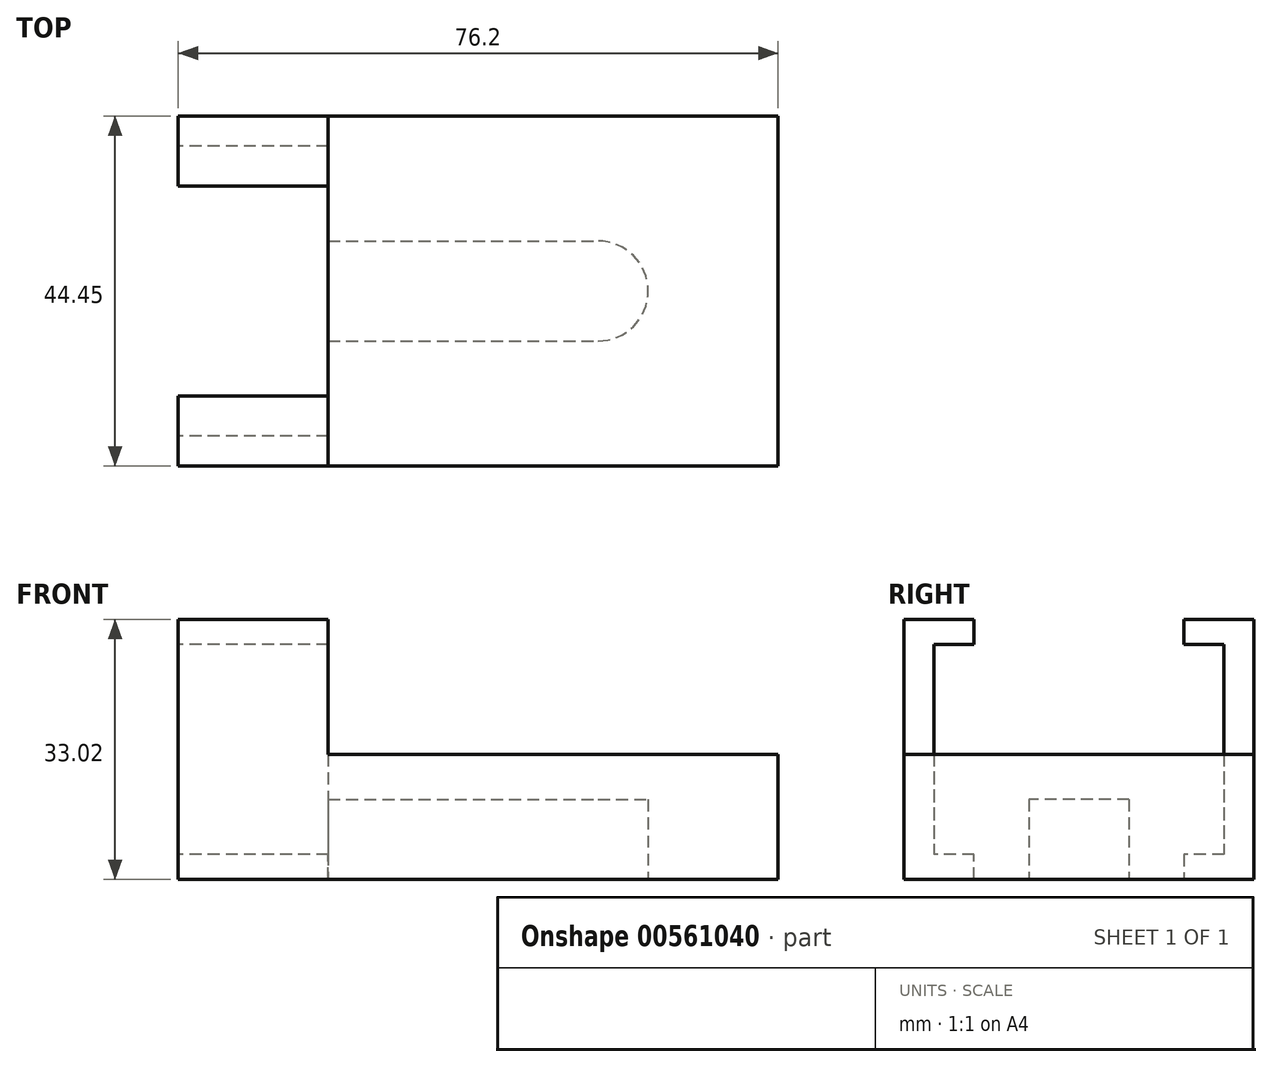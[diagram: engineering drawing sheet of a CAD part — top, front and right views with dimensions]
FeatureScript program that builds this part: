
annotation { "Feature Type Name" : "Feature", "Feature Type Description" : "" }
export const myFeature = defineFeature(function(context is Context, id is Id, definition is map)
    precondition{}
    {
        {
            var Q0;
            Q0=qCreatedBy(makeId("Top.planeOp"),FACE);
            var sketch = newSketch(context, id + "F0", { "sketchPlane" : qUnion([Q0])});
            skLineSegment(sketch, "E0", {"start": v(0, 0) * mm, "end": v(76.2, 0) * mm});
            skLineSegment(sketch, "E1", {"start": v(76.2, 0) * mm, "end": v(76.2, 44.45) * mm});
            skLineSegment(sketch, "E2", {"start": v(76.2, 44.45) * mm, "end": v(0, 44.45) * mm});
            skLineSegment(sketch, "E3", {"start": v(0, 44.45) * mm, "end": v(0, 0) * mm});
            skSolve(sketch);
        }
        {
            var Q0;
            Q0=makeQuery(id+"F0.imprint","IMPRINT",FACE,{"disambiguationData":[TD([[makeQuery(id+"F0.imprint","IMPRINT",EDGE,{"derivedFrom":sQuery(id+"F0.wireOp",EDGE,"E0")}),1.0]])]});
            extrude(context, id + "F1", {"entities" : qUnion([Q0]), "depth" : 33.02 * mm, "offsetDistance" : 25.4 * mm});
        }
        {
            var Q0;
            Q0=makeQuery(id+"F1.opExtrude","CAP_FACE",FACE,{"disambiguationData":[OSD([sQuery(id+"F0.wireOp",EDGE,"E0"),sQuery(id+"F0.wireOp",EDGE,"E1"),sQuery(id+"F0.wireOp",EDGE,"E2"),sQuery(id+"F0.wireOp",EDGE,"E3")])],"isStart":false});
            var sketch = newSketch(context, id + "F2", { "sketchPlane" : qUnion([Q0])});
            skLineSegment(sketch, "E4.bottom", {"start": v(76.2, 44.45) * mm, "end": v(19.05, 44.45) * mm});
            skLineSegment(sketch, "E4.top", {"start": v(76.2, 0) * mm, "end": v(19.05, 0) * mm});
            skLineSegment(sketch, "E4.left", {"start": v(76.2, 44.45) * mm, "end": v(76.2, 0) * mm});
            skLineSegment(sketch, "E4.right", {"start": v(19.05, 44.45) * mm, "end": v(19.05, 0) * mm});
            skSolve(sketch);
        }
        {
            var Q0;
            Q0=makeQuery(id+"F2.imprint","IMPRINT",FACE,{"disambiguationData":[TD([[makeQuery(id+"F2.imprint","IMPRINT",EDGE,{"derivedFrom":sQuery(id+"F2.wireOp",EDGE,"E4.bottom")}),1.0]])]});
            extrude(context, id + "F3", {"entities" : qUnion([Q0]), "operationType" : NewBodyOperationType.REMOVE, "oppositeDirection" : true, "depth" : 17.14 * mm, "offsetDistance" : 25.4 * mm});
        }
        {
            var Q0;
            Q0=makeQuery(id+"F1.opExtrude","SWEPT_FACE",FACE,{"disambiguationData":[OSD([sQuery(id+"F0.wireOp",EDGE,"E3")])]});
            var sketch = newSketch(context, id + "F4", { "sketchPlane" : qUnion([Q0])});
            skLineSegment(sketch, "E5.bottom", {"start": v(-40.64, 29.85) * mm, "end": v(-3.81, 29.85) * mm});
            skLineSegment(sketch, "E5.top", {"start": v(-40.64, 3.18) * mm, "end": v(-3.81, 3.18) * mm});
            skLineSegment(sketch, "E5.left", {"start": v(-40.64, 29.85) * mm, "end": v(-40.64, 3.18) * mm});
            skLineSegment(sketch, "E5.right", {"start": v(-3.81, 29.85) * mm, "end": v(-3.81, 3.18) * mm});
            skLineSegment(sketch, "E6", {"start": v(-35.56, 29.85) * mm, "end": v(-35.56, 33.02) * mm});
            skLineSegment(sketch, "E7", {"start": v(-35.56, 33.02) * mm, "end": v(-8.9, 33.02) * mm});
            skLineSegment(sketch, "E8", {"start": v(-8.9, 33.02) * mm, "end": v(-8.9, 29.85) * mm});
            skLineSegment(sketch, "E9", {"start": v(-35.56, 3.17) * mm, "end": v(-35.56, 0) * mm});
            skLineSegment(sketch, "E10", {"start": v(-35.56, 0) * mm, "end": v(-8.9, 0) * mm});
            skLineSegment(sketch, "E11", {"start": v(-8.9, 0) * mm, "end": v(-8.9, 3.18) * mm});
            skSolve(sketch);
        }
        {
            var Q0;
            {var subQ0=sQuery(id+"F4.wireOp",EDGE,"E5.left");Q0=makeQuery(id+"F4.imprint","IMPRINT",FACE,{"disambiguationData":[TD([[makeQuery(id+"F4.imprint","IMPRINT",EDGE,{"derivedFrom":subQ0}),1.0]])]});}
            var Q1;
            {var subQ0=sQuery(id+"F4.wireOp",EDGE,"E6");Q1=makeQuery(id+"F4.imprint","IMPRINT",FACE,{"disambiguationData":[TD([[makeQuery(id+"F4.imprint","IMPRINT",EDGE,{"derivedFrom":subQ0}),-1.0]])]});}
            var Q2;
            {var subQ0=sQuery(id+"F4.wireOp",EDGE,"E9");Q2=makeQuery(id+"F4.imprint","IMPRINT",FACE,{"disambiguationData":[TD([[makeQuery(id+"F4.imprint","IMPRINT",EDGE,{"derivedFrom":subQ0}),1.0]])]});}
            extrude(context, id + "F5", {"entities" : qUnion([Q0, Q1, Q2]), "operationType" : NewBodyOperationType.REMOVE, "oppositeDirection" : true, "depth" : 19.05 * mm, "offsetDistance" : 25.4 * mm});
        }
        {
            var Q0;
            Q0=makeQuery(id+"F1.opExtrude","CAP_FACE",FACE,{"disambiguationData":[OSD([sQuery(id+"F0.wireOp",EDGE,"E0"),sQuery(id+"F0.wireOp",EDGE,"E1"),sQuery(id+"F0.wireOp",EDGE,"E2"),sQuery(id+"F0.wireOp",EDGE,"E3")])],"isStart":true});
            var sketch = newSketch(context, id + "F6", { "sketchPlane" : qUnion([Q0])});
            skLineSegment(sketch, "E12.bottom", {"start": v(19.05, -15.88) * mm, "end": v(53.34, -15.88) * mm});
            skLineSegment(sketch, "E12.top", {"start": v(19.05, -28.58) * mm, "end": v(53.34, -28.57) * mm});
            skLineSegment(sketch, "E12.left", {"start": v(19.05, -15.88) * mm, "end": v(19.05, -28.57) * mm});
            skLineSegment(sketch, "E12.right", {"start": v(53.34, -15.87) * mm, "end": v(53.34, -28.58) * mm});
            skArc(sketch, "E13", {"start": v(53.34, -15.87) * mm, "mid": v(59.7, -22.22) * mm, "end": v(53.34, -28.57) * mm});
            skSolve(sketch);
        }
        {
            var Q0;
            Q0=makeQuery(id+"F6.imprint","IMPRINT",FACE,{"disambiguationData":[TD([[makeQuery(id+"F6.imprint","IMPRINT",EDGE,{"derivedFrom":sQuery(id+"F6.wireOp",EDGE,"E12.right")}),1.0]])]});
            var Q1;
            Q1=makeQuery(id+"F6.imprint","IMPRINT",FACE,{"disambiguationData":[TD([[makeQuery(id+"F6.imprint","IMPRINT",EDGE,{"derivedFrom":sQuery(id+"F6.wireOp",EDGE,"E12.bottom")}),-1.0]])]});
            extrude(context, id + "F7", {"entities" : qUnion([Q0, Q1]), "operationType" : NewBodyOperationType.REMOVE, "oppositeDirection" : true, "depth" : 10.16 * mm, "offsetDistance" : 25.4 * mm});
        }
    });
